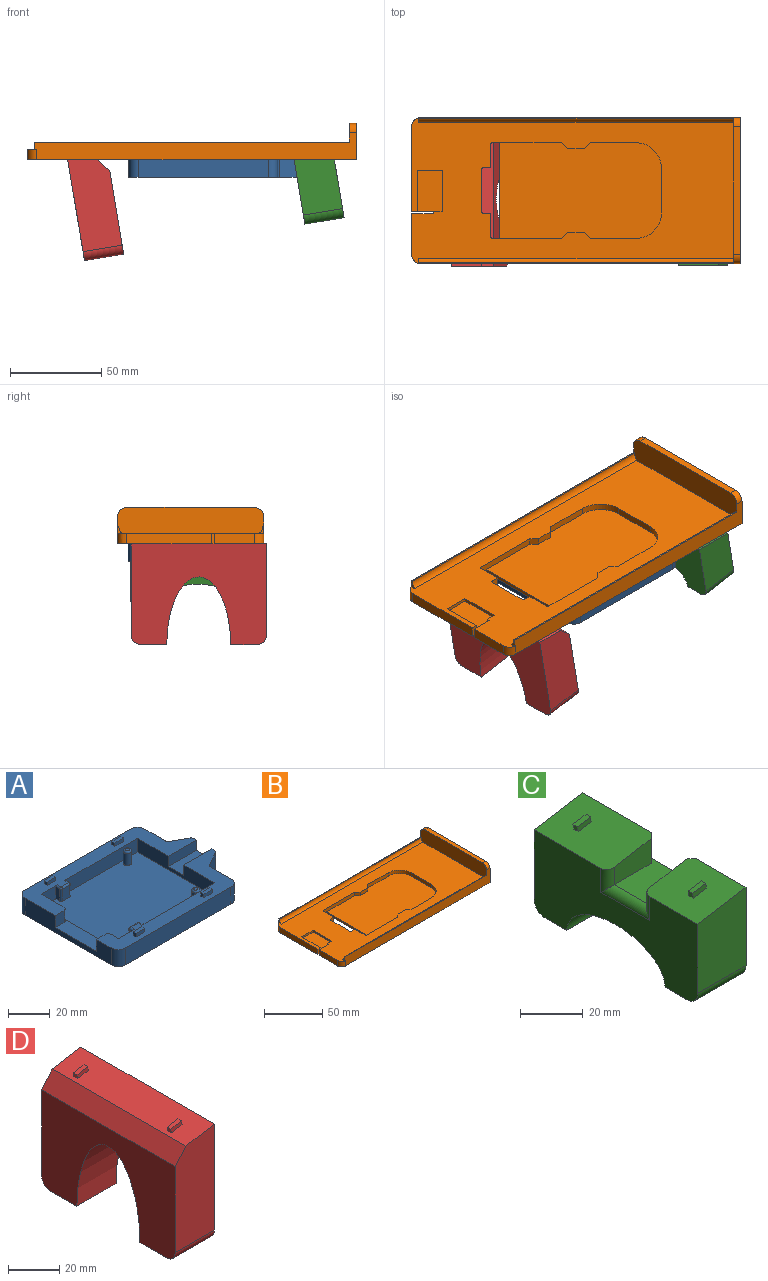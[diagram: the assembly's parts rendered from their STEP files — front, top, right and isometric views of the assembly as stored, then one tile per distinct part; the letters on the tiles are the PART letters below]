
ASSEMBLY  parts=4 mates=3
PART A: 80 faces, bbox 92.6x68.5x12 mm
  f0: plane 65.5x52.5mm, normal (0,0,1), area 3365.5mm2, adj f2,f3,f4,f5,f6,f7,f8,f9
  f1: plane 92.58x68.5mm, normal (0,0,-1), area 5808.1mm2, adj f12,f13,f14,f15,f16,f28,f29,f30
  f2: plane 11x8mm, normal (0,-1,0), area 80.2mm2, adj f0,f3,f6,f18,f73
  f3: plane 52.5x8mm, normal (1,0,0), area 196mm2, adj f0,f2,f18,f19,f31,f37,f66,f67
  f4: plane 52.5x8mm, normal (-1,0,0), area 357mm2, adj f0,f5,f11,f18,f20,f21,f31,f36
  f5: plane 49.5x8mm, normal (0,-1,0), area 388.2mm2, adj f0,f4,f10,f18,f76
  f6: plane 7x2.5mm, normal (-1,0,0), area 17.5mm2, adj f0,f2,f7,f73
  f7: cylinder r=1mm len=7mm, axis (0,0,-1), area 11mm2, adj f0,f6,f8,f74
  f8: plane 7x5mm, normal (0,-1,0), area 35mm2, adj f0,f7,f9,f75
  f9: cylinder r=1mm len=7mm, axis (0,0,-1), area 11mm2, adj f0,f8,f10,f77
  f10: plane 7x2.5mm, normal (1,0,0), area 17.5mm2, adj f0,f5,f9,f76
  f11: plane 19.08x6mm, normal (0,-1,0), area 114.5mm2, adj f4,f12,f18,f36
  f12: plane 13.79x10mm, normal (1,0,0), area 74.9mm2, adj f1,f11,f18,f21,f31,f36,f62,f65
  f13: plane 10x9.02mm, normal (0.48,0.88,0), area 103mm2, adj f1,f18,f64,f65
  f14: plane 13.87x10mm, normal (1,0,0), area 138.7mm2, adj f1,f18,f60,f64
  f15: plane 71.5x10mm, normal (0,1,0), area 715mm2, adj f1,f18,f60,f61
  f16: plane 58.5x10mm, normal (-1,0,0), area 389mm2, adj f1,f17,f18,f27,f31,f37,f59,f61
  f17: plane 7x6mm, normal (0,-1,0), area 42mm2, adj f16,f18,f37,f67
  f18: plane 92.58x29mm, normal (0,0,1), area 1002.1mm2, adj f2,f3,f4,f5,f11,f12,f13,f14
  f19: plane 11x8mm, normal (0,1,0), area 80.2mm2, adj f0,f3,f26,f31,f68
  f20: plane 49.5x8mm, normal (0,1,0), area 388.2mm2, adj f0,f4,f22,f31,f71
  f21: plane 19.08x6mm, normal (0,1,0), area 114.5mm2, adj f4,f12,f31,f36
  f22: plane 7x2.5mm, normal (1,0,0), area 17.5mm2, adj f0,f20,f23,f71
  f23: cylinder r=1mm len=7mm, axis (0,0,-1), area 11mm2, adj f0,f22,f24,f72
  f24: plane 7x5mm, normal (0,1,0), area 35mm2, adj f0,f23,f25,f70
  f25: cylinder r=1mm len=7mm, axis (0,0,-1), area 11mm2, adj f0,f24,f26,f69
  f26: plane 7x2.5mm, normal (-1,0,0), area 17.5mm2, adj f0,f19,f25,f68
  f27: plane 7x6mm, normal (0,1,0), area 42mm2, adj f16,f31,f37,f66
  f28: plane 71.5x10mm, normal (0,-1,0), area 715mm2, adj f1,f31,f58,f59
  f29: plane 13.87x10mm, normal (1,0,0), area 138.7mm2, adj f1,f31,f58,f63
  f30: plane 10x9.02mm, normal (0.48,-0.88,0), area 103mm2, adj f1,f31,f62,f63
  f31: plane 92.58x29mm, normal (0,0,1), area 918.1mm2, adj f3,f4,f12,f16,f19,f20,f21,f27
  f32: cylinder r=2mm len=7mm, axis (0,0,-1), area 88mm2, adj f0,f79
  f33: plane 2x2mm, normal (0,0,1), area 3.1mm2, adj f79
  f34: cylinder r=2mm len=7mm, axis (0,0,-1), area 88mm2, adj f0,f78
  f35: plane 2x2mm, normal (0,0,1), area 3.1mm2, adj f78
  f36: plane 19.08x10.5mm, normal (0,0,1), area 200.4mm2, adj f4,f11,f12,f21
  f37: plane 32x8mm, normal (0,0,1), area 225.7mm2, adj f3,f16,f17,f27,f66,f67
  f38: plane 6x2mm, normal (0,0,1), area 12mm2, adj f39,f40,f41,f42
  f39: plane 2x2mm, normal (1,0,0), area 4mm2, adj f31,f38,f40,f42
  f40: plane 6x2mm, normal (0,-1,0), area 12mm2, adj f31,f38,f39,f41
  f41: plane 2x2mm, normal (-1,0,0), area 4mm2, adj f31,f38,f40,f42
  f42: plane 6x2mm, normal (0,1,0), area 12mm2, adj f31,f38,f39,f41
  f43: plane 6x2mm, normal (0,0,1), area 12mm2, adj f44,f45,f46,f47
  f44: plane 2x2mm, normal (1,0,0), area 4mm2, adj f31,f43,f45,f47
  f45: plane 6x2mm, normal (0,-1,0), area 12mm2, adj f31,f43,f44,f46
  f46: plane 2x2mm, normal (-1,0,0), area 4mm2, adj f31,f43,f45,f47
  f47: plane 6x2mm, normal (0,1,0), area 12mm2, adj f31,f43,f44,f46
  f48: plane 6x2mm, normal (0,0,1), area 12mm2, adj f49,f50,f51,f52
  f49: plane 6x2mm, normal (0,1,0), area 12mm2, adj f18,f48,f50,f52
  f50: plane 2x2mm, normal (1,0,0), area 4mm2, adj f18,f48,f49,f51
  f51: plane 6x2mm, normal (0,-1,0), area 12mm2, adj f18,f48,f50,f52
  f52: plane 2x2mm, normal (-1,0,0), area 4mm2, adj f18,f48,f49,f51
  f53: plane 6x2mm, normal (0,0,1), area 12mm2, adj f54,f55,f56,f57
  f54: plane 6x2mm, normal (0,1,0), area 12mm2, adj f18,f53,f55,f57
  f55: plane 2x2mm, normal (1,0,0), area 4mm2, adj f18,f53,f54,f56
  f56: plane 6x2mm, normal (0,-1,0), area 12mm2, adj f18,f53,f55,f57
  f57: plane 2x2mm, normal (-1,0,0), area 4mm2, adj f18,f53,f54,f56
  f58: cylinder r=5mm len=10mm, axis (0,0,1), area 78.5mm2, adj f1,f28,f29,f31
  f59: cylinder r=5mm len=10mm, axis (0,0,-1), area 78.5mm2, adj f1,f16,f28,f31
  f60: cylinder r=5mm len=10mm, axis (0,0,-1), area 78.5mm2, adj f1,f14,f15,f18
  f61: cylinder r=5mm len=10mm, axis (0,0,1), area 78.5mm2, adj f1,f15,f16,f18
  f62: cylinder r=2mm len=10mm, axis (0,0,1), area 21.3mm2, adj f1,f12,f30,f31
  f63: cylinder r=2mm len=10mm, axis (0,0,1), area 21.3mm2, adj f1,f29,f30,f31
  f64: cylinder r=2mm len=10mm, axis (0,0,-1), area 21.3mm2, adj f1,f13,f14,f18
  f65: cylinder r=2mm len=10mm, axis (0,0,-1), area 21.3mm2, adj f1,f12,f13,f18
  f66: cylinder r=2mm len=7mm, axis (0,0,-1), area 22mm2, adj f3,f27,f31,f37
  f67: cylinder r=2mm len=7mm, axis (0,0,1), area 22mm2, adj f3,f17,f18,f37
  f68: cylinder r=1mm len=2.5mm, axis (0,1,0), area 3.9mm2, adj f19,f26,f31,f69
  f69: sphere r=1mm, area 1.6mm2, adj f25,f68,f70
  f70: cylinder r=1mm len=5mm, axis (1,0,0), area 7.9mm2, adj f24,f31,f69,f72
  f71: cylinder r=1mm len=2.5mm, axis (0,-1,0), area 3.9mm2, adj f20,f22,f31,f72
  f72: sphere r=1mm, area 1.6mm2, adj f23,f70,f71
  f73: cylinder r=1mm len=2.5mm, axis (0,1,0), area 3.9mm2, adj f2,f6,f18,f74
  f74: sphere r=1mm, area 1.6mm2, adj f7,f73,f75
  f75: cylinder r=1mm len=5mm, axis (-1,0,0), area 7.9mm2, adj f8,f18,f74,f77
  f76: cylinder r=1mm len=2.5mm, axis (0,-1,0), area 3.9mm2, adj f5,f10,f18,f77
  f77: sphere r=1mm, area 1.6mm2, adj f9,f75,f76
  f78: torus R=1mm, axis (0,0,1), area 16.2mm2, adj f34,f35
  f79: torus R=1mm, axis (0,0,1), area 16.2mm2, adj f32,f33
PART B: 93 faces, bbox 180x80x20 mm
  f0: plane 180x80mm, normal (0,0,-1), area 13875.2mm2, adj f3,f5,f11,f12,f13,f14,f15,f16
  f1: plane 80x14.3mm, normal (-1,0,0), area 1123.4mm2, adj f26,f37,f39,f41,f43,f45,f47,f48
  f2: plane 4.9x1.7mm, normal (0,1,0), area 8.3mm2, adj f32,f33,f39,f42
  f3: plane 52.5x2mm, normal (-1,0,0), area 105mm2, adj f0,f4,f5,f20
  f4: plane 88.5x52.5mm, normal (0,0,1), area 4480.9mm2, adj f3,f5,f6,f7,f8,f9,f10,f20
  f5: plane 37.75x5.7mm, normal (0,1,0), area 147.7mm2, adj f0,f3,f4,f11,f38,f39
  f6: plane 24.75x3.7mm, normal (0,1,0), area 91.6mm2, adj f4,f10,f24,f39
  f7: plane 24.5x3.7mm, normal (-1,0,0), area 90.6mm2, adj f4,f9,f10,f39
  f8: plane 24.75x3.7mm, normal (0,-1,0), area 91.6mm2, adj f4,f9,f23,f39
  f9: cylinder r=14mm len=14mm, axis (0,0,-1), area 81.4mm2, adj f4,f7,f8,f39
  f10: cylinder r=14mm len=14mm, axis (0,0,-1), area 81.4mm2, adj f4,f6,f7,f39
  f11: cylinder r=1mm len=5.7mm, axis (0,0,-1), area 9mm2, adj f0,f5,f12,f39
  f12: plane 12.75x5.7mm, normal (1,0,0), area 72.7mm2, adj f0,f11,f13,f39
  f13: plane 5.7x4mm, normal (0,1,0), area 22.8mm2, adj f0,f12,f14,f39
  f14: cylinder r=1mm len=5.7mm, axis (0,0,-1), area 9mm2, adj f0,f13,f15,f39
  f15: plane 23x5.7mm, normal (1,0,0), area 131.1mm2, adj f0,f14,f16,f39
  f16: cylinder r=1mm len=5.7mm, axis (0,0,-1), area 9mm2, adj f0,f15,f17,f39
  f17: plane 5.7x4mm, normal (0,-1,0), area 22.8mm2, adj f0,f16,f18,f39
  f18: plane 12.75x5.7mm, normal (1,0,0), area 72.7mm2, adj f0,f17,f19,f39
  f19: cylinder r=1mm len=5.7mm, axis (0,0,-1), area 9mm2, adj f0,f18,f20,f39
  f20: plane 37.75x5.7mm, normal (0,-1,0), area 147.7mm2, adj f0,f3,f4,f19,f21,f39
  f21: plane 3.7x3.5mm, normal (-0.68,-0.73,0), area 17.7mm2, adj f4,f20,f22,f39
  f22: plane 9x3.7mm, normal (0,-1,0), area 33.3mm2, adj f4,f21,f23,f39
  f23: plane 3.7x3.5mm, normal (0.68,-0.73,0), area 17.7mm2, adj f4,f8,f22,f39
  f24: plane 3.7x3.5mm, normal (0.68,0.73,0), area 17.7mm2, adj f4,f6,f25,f39
  f25: plane 9x3.7mm, normal (0,1,0), area 33.3mm2, adj f4,f24,f38,f39
  f26: plane 176x15mm, normal (0,1,0), area 1722.7mm2, adj f0,f1,f27,f40,f43,f44,f46,f92
  f27: cylinder r=5mm len=5.7mm, axis (0,0,-1), area 44.8mm2, adj f0,f26,f28,f39,f44
  f28: plane 46.25x5.7mm, normal (-1,0,0), area 263.6mm2, adj f0,f27,f29,f39
  f29: plane 11.87x5.7mm, normal (0,-1,0), area 52.5mm2, adj f0,f28,f30,f33,f39,f42
  f30: plane 22.5x1.7mm, normal (1,0,0), area 38.2mm2, adj f29,f31,f39,f42
  f31: plane 13.8x1.7mm, normal (0,-1,0), area 23.5mm2, adj f30,f32,f39,f42
  f32: plane 22.5x1.7mm, normal (-1,0,0), area 38.2mm2, adj f2,f31,f39,f42
  f33: plane 5.7x1.55mm, normal (-1,0,0), area 8.8mm2, adj f0,f2,f29,f34,f39
  f34: plane 11.87x5.7mm, normal (0,1,0), area 67.6mm2, adj f0,f33,f35,f39
  f35: plane 22.2x5.7mm, normal (-1,0,0), area 126.6mm2, adj f0,f34,f36,f39
  f36: cylinder r=5mm len=5.7mm, axis (0,0,-1), area 44.8mm2, adj f0,f35,f37,f39,f49
  f37: plane 176x15mm, normal (0,-1,0), area 1722.7mm2, adj f0,f1,f36,f40,f47,f49,f50,f91
  f38: plane 3.7x3.5mm, normal (-0.68,0.73,0), area 17.7mm2, adj f4,f5,f25,f39
  f39: plane 176x79.8mm, normal (0,0,1), area 7966.4mm2, adj f1,f2,f5,f6,f7,f8,f9,f10
  f40: plane 80x20mm, normal (1,0,0), area 1589.3mm2, adj f0,f26,f37,f41,f91,f92
  f41: plane 70x4mm, normal (0,0,1), area 280mm2, adj f1,f40,f91,f92
  f42: plane 22.5x13.8mm, normal (0,0,1), area 310.5mm2, adj f2,f29,f30,f31,f32
  f43: plane 172x0.67mm, normal (0,0,1), area 116mm2, adj f1,f26,f45,f46
  f44: plane 1x0.1mm, normal (0,0,-1), area 0mm2, adj f26,f27,f46
  f45: cylinder r=4.71mm len=172mm, axis (1,0,0), area 798mm2, adj f1,f39,f43,f46
  f46: plane 4x2.64mm, normal (-1,0,0), area 4.9mm2, adj f26,f39,f43,f44,f45
  f47: plane 172x0.67mm, normal (0,0,1), area 116mm2, adj f1,f37,f48,f50
  f48: cylinder r=4.71mm len=172mm, axis (1,0,0), area 798mm2, adj f1,f39,f47,f50
  f49: plane 1x0.1mm, normal (0,0,-1), area 0mm2, adj f36,f37,f50
  f50: plane 4x2.64mm, normal (-1,0,0), area 4.9mm2, adj f37,f39,f47,f48,f49
  f51: plane 2.5x2.2mm, normal (1,0,0), area 5.5mm2, adj f0,f52,f54,f55
  f52: plane 6.2x2.5mm, normal (0,1,0), area 15.5mm2, adj f0,f51,f53,f55
  f53: plane 2.5x2.2mm, normal (-1,0,0), area 5.5mm2, adj f0,f52,f54,f55
  f54: plane 6.2x2.5mm, normal (0,-1,0), area 15.5mm2, adj f0,f51,f53,f55
  f55: plane 6.2x2.2mm, normal (0,0,-1), area 13.6mm2, adj f51,f52,f53,f54
  f56: plane 6.2x2.5mm, normal (0,1,0), area 15.5mm2, adj f0,f57,f59,f60
  f57: plane 2.5x2.2mm, normal (-1,0,0), area 5.5mm2, adj f0,f56,f58,f60
  f58: plane 6.2x2.5mm, normal (0,-1,0), area 15.5mm2, adj f0,f57,f59,f60
  f59: plane 2.5x2.2mm, normal (1,0,0), area 5.5mm2, adj f0,f56,f58,f60
  f60: plane 6.2x2.2mm, normal (0,0,-1), area 13.6mm2, adj f56,f57,f58,f59
  f61: plane 2.5x2.2mm, normal (1,0,0), area 5.5mm2, adj f0,f62,f64,f65
  f62: plane 6.2x2.5mm, normal (0,1,0), area 15.5mm2, adj f0,f61,f63,f65
  f63: plane 2.5x2.2mm, normal (-1,0,0), area 5.5mm2, adj f0,f62,f64,f65
  f64: plane 6.2x2.5mm, normal (0,-1,0), area 15.5mm2, adj f0,f61,f63,f65
  f65: plane 6.2x2.2mm, normal (0,0,-1), area 13.6mm2, adj f61,f62,f63,f64
  f66: plane 6.2x2.5mm, normal (0,1,0), area 15.5mm2, adj f0,f67,f69,f70
  f67: plane 2.5x2.2mm, normal (-1,0,0), area 5.5mm2, adj f0,f66,f68,f70
  f68: plane 6.2x2.5mm, normal (0,-1,0), area 15.5mm2, adj f0,f67,f69,f70
  f69: plane 2.5x2.2mm, normal (1,0,0), area 5.5mm2, adj f0,f66,f68,f70
  f70: plane 6.2x2.2mm, normal (0,0,-1), area 13.6mm2, adj f66,f67,f68,f69
  f71: plane 2.5x2.2mm, normal (1,0,0), area 5.5mm2, adj f0,f72,f74,f75
  f72: plane 6.2x2.5mm, normal (0,1,0), area 15.5mm2, adj f0,f71,f73,f75
  f73: plane 2.5x2.2mm, normal (-1,0,0), area 5.5mm2, adj f0,f72,f74,f75
  f74: plane 6.2x2.5mm, normal (0,-1,0), area 15.5mm2, adj f0,f71,f73,f75
  f75: plane 6.2x2.2mm, normal (0,0,-1), area 13.6mm2, adj f71,f72,f73,f74
  f76: plane 2.5x2.2mm, normal (1,0,0), area 5.5mm2, adj f0,f77,f79,f80
  f77: plane 6.2x2.5mm, normal (0,1,0), area 15.5mm2, adj f0,f76,f78,f80
  f78: plane 2.5x2.2mm, normal (-1,0,0), area 5.5mm2, adj f0,f77,f79,f80
  f79: plane 6.2x2.5mm, normal (0,-1,0), area 15.5mm2, adj f0,f76,f78,f80
  f80: plane 6.2x2.2mm, normal (0,0,-1), area 13.6mm2, adj f76,f77,f78,f79
  f81: plane 6.2x2.5mm, normal (0,-1,0), area 15.5mm2, adj f0,f82,f84,f85
  f82: plane 2.5x2.2mm, normal (1,0,0), area 5.5mm2, adj f0,f81,f83,f85
  f83: plane 6.2x2.5mm, normal (0,1,0), area 15.5mm2, adj f0,f82,f84,f85
  f84: plane 2.5x2.2mm, normal (-1,0,0), area 5.5mm2, adj f0,f81,f83,f85
  f85: plane 6.2x2.2mm, normal (0,0,-1), area 13.6mm2, adj f81,f82,f83,f84
  f86: plane 2.5x2.2mm, normal (-1,0,0), area 5.5mm2, adj f0,f87,f89,f90
  f87: plane 6.2x2.5mm, normal (0,-1,0), area 15.5mm2, adj f0,f86,f88,f90
  f88: plane 2.5x2.2mm, normal (1,0,0), area 5.5mm2, adj f0,f87,f89,f90
  f89: plane 6.2x2.5mm, normal (0,1,0), area 15.5mm2, adj f0,f86,f88,f90
  f90: plane 6.2x2.2mm, normal (0,0,-1), area 13.6mm2, adj f86,f87,f88,f89
  f91: cylinder r=5mm len=5mm, axis (-1,0,0), area 31.4mm2, adj f1,f37,f40,f41
  f92: cylinder r=5mm len=5mm, axis (1,0,0), area 31.4mm2, adj f1,f26,f40,f41
PART C: 29 faces, bbox 21.7x74x36.2 mm
  f0: plane 21.7x9.84mm, normal (0,0,-1), area 213.5mm2, adj f1,f9,f14,f23
  f1: plane 74x35.59mm, normal (1,0,0), area 1960.3mm2, adj f0,f2,f10,f11,f12,f13,f14,f15
  f2: plane 33.2x21.7mm, normal (-0.16,0,0.99), area 714.4mm2, adj f1,f5,f7,f9,f13,f16,f18,f22
  f3: plane 5.92x2mm, normal (-0.16,0,0.99), area 12mm2, adj f5,f7,f16,f18
  f4: plane 5.92x2mm, normal (-0.16,0,0.99), area 12mm2, adj f6,f8,f17,f19
  f5: plane 2x1.97mm, normal (-0.99,0,-0.16), area 4mm2, adj f2,f3,f16,f18
  f6: plane 2x1.97mm, normal (-0.99,0,-0.16), area 4mm2, adj f4,f11,f17,f19
  f7: plane 2x1.97mm, normal (0.99,0,0.16), area 4mm2, adj f2,f3,f16,f18
  f8: plane 2x1.97mm, normal (0.99,0,0.16), area 4mm2, adj f4,f11,f17,f19
  f9: plane 74x31.97mm, normal (-1,0,0), area 1686.3mm2, adj f0,f2,f10,f11,f12,f13,f14,f15
  f10: plane 21.7x9.84mm, normal (0,0,-1), area 213.5mm2, adj f1,f9,f15,f23
  f11: plane 24.8x21.7mm, normal (-0.16,0,0.99), area 529.6mm2, adj f1,f6,f8,f9,f12,f17,f19,f21
  f12: plane 30.59x21.7mm, normal (0,-1,0), area 624.6mm2, adj f1,f9,f11,f15
  f13: plane 30.59x21.7mm, normal (0,1,0), area 624.6mm2, adj f1,f2,f9,f14
  f14: cylinder r=5mm len=21.7mm, axis (1,0,0), area 170.4mm2, adj f0,f1,f9,f13
  f15: cylinder r=5mm len=21.7mm, axis (-1,0,0), area 170.4mm2, adj f1,f9,f10,f12
  f16: plane 6.25x2.96mm, normal (0,1,0), area 12mm2, adj f2,f3,f5,f7
  f17: plane 6.25x2.96mm, normal (0,-1,0), area 12mm2, adj f4,f6,f8,f11
  f18: plane 6.25x2.96mm, normal (0,-1,0), area 12mm2, adj f2,f3,f5,f7
  f19: plane 6.25x2.96mm, normal (0,1,0), area 12mm2, adj f4,f6,f8,f11
  f20: plane 20x18.7mm, normal (0,0,1), area 303.2mm2, adj f1,f21,f22,f26,f27,f28
  f21: plane 16.7x9.67mm, normal (0,1,0), area 138.2mm2, adj f11,f20,f24,f28
  f22: plane 16.7x9.67mm, normal (0,-1,0), area 138.2mm2, adj f2,f20,f25,f27
  f23: extruded ~44.32x21.7mm, area 1227.4mm2, adj f0,f1,f9,f10
  f24: cylinder r=3mm len=9.88mm, axis (0,0,-1), area 36.1mm2, adj f9,f11,f21,f26
  f25: cylinder r=3mm len=9.88mm, axis (0,0,1), area 36.1mm2, adj f2,f9,f22,f26
  f26: cylinder r=3mm len=22mm, axis (0,1,0), area 85.7mm2, adj f9,f20,f24,f25
  f27: plane 10x2mm, normal (0.71,-0.71,0), area 27.8mm2, adj f1,f2,f20,f22
  f28: plane 10x2mm, normal (0.71,0.71,0), area 27.8mm2, adj f1,f11,f20,f21
PART D: 21 faces, bbox 21.7x74x56.5 mm
  f0: plane 2x1.97mm, normal (-0.99,0,-0.16), area 4mm2, adj f9,f11,f16,f18
  f1: plane 2x1.97mm, normal (-0.99,0,-0.16), area 4mm2, adj f3,f9,f17,f19
  f2: plane 2x1.97mm, normal (0.99,0,0.16), area 4mm2, adj f3,f9,f17,f19
  f3: plane 5.92x2mm, normal (-0.16,0,0.99), area 12mm2, adj f1,f2,f17,f19
  f4: plane 50.81x21.7mm, normal (0,1,0), area 1045.6mm2, adj f6,f7,f9,f13,f20
  f5: plane 21.7x14.5mm, normal (0,0,-1), area 314.7mm2, adj f6,f7,f13,f15
  f6: plane 74x55.81mm, normal (1,0,0), area 3088.4mm2, adj f4,f5,f8,f9,f12,f13,f14,f15
  f7: plane 74x46.19mm, normal (-1,0,0), area 2376.8mm2, adj f4,f5,f8,f12,f13,f14,f15,f20
  f8: plane 21.7x14.5mm, normal (0,0,-1), area 314.7mm2, adj f6,f7,f14,f15
  f9: plane 74x15.78mm, normal (-0.16,0,0.99), area 1160mm2, adj f0,f1,f2,f4,f6,f10,f12,f16
  f10: plane 2x1.97mm, normal (0.99,0,0.16), area 4mm2, adj f9,f11,f16,f18
  f11: plane 5.92x2mm, normal (-0.16,0,0.99), area 12mm2, adj f0,f10,f16,f18
  f12: plane 50.81x21.7mm, normal (0,-1,0), area 1045.6mm2, adj f6,f7,f9,f14,f20
  f13: cylinder r=5mm len=21.7mm, axis (1,0,0), area 170.4mm2, adj f4,f5,f6,f7
  f14: cylinder r=5mm len=21.7mm, axis (-1,0,0), area 170.4mm2, adj f6,f7,f8,f12
  f15: extruded ~37.5x35mm, area 1937.3mm2, adj f5,f6,f7,f8
  f16: plane 6.25x2.96mm, normal (0,1,0), area 12mm2, adj f0,f9,f10,f11
  f17: plane 6.25x2.96mm, normal (0,-1,0), area 12mm2, adj f1,f2,f3,f9
  f18: plane 6.25x2.96mm, normal (0,-1,0), area 12mm2, adj f0,f9,f10,f11
  f19: plane 6.25x2.96mm, normal (0,1,0), area 12mm2, adj f1,f2,f3,f9
  f20: plane 74x6.99mm, normal (-0.76,0,0.65), area 677.6mm2, adj f4,f7,f9,f12
PLACE A t=(63.45,66.25,-9.5)mm
PLACE B at identity fixed
PLACE C rot(axis=(0.08,0,-1),180deg) t=(184.93,-1.05,-29.59)mm
PLACE D rot(axis=(0.08,0,-1),180deg) t=(183.93,-1.45,-29.59)mm
MATE fastened C.f11 <-> B.f0  axis (0,0,1) through (160,62.95,0)mm
MATE fastened D.f9 <-> B.f0  axis (0,0,1) through (30,8.55,0)mm
MATE slider A.f43 <-> B.f75  axis (0,0,1) through (116.45,10.75,2.5)mm
